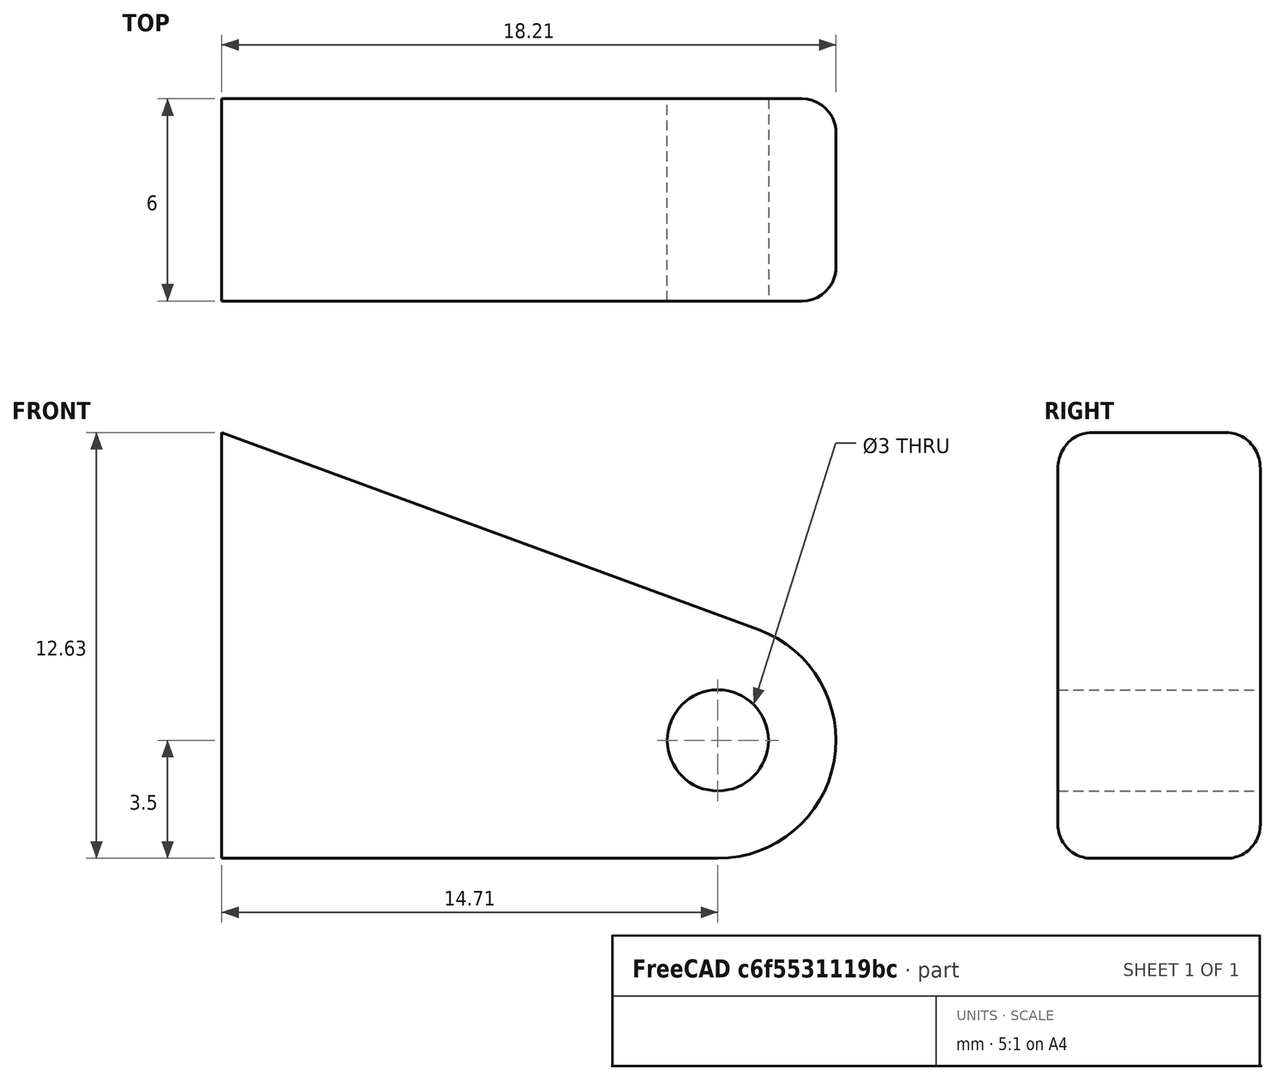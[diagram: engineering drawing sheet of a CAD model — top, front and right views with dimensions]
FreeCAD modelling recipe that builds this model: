
FCSTD DOCUMENT  (FreeCAD 0.16R6704 (Git))
Label: txerritxo
License: All rights reserved
LicenseURL: http://en.wikipedia.org/wiki/All_rights_reserved
objects: PartDesign::Fillet×2, Mesh::Feature×1, Part::Feature×1, Sketcher::SketchObject×1, PartDesign::Pad×1
note: 6 computed .brp shape members not serialized (recipe doc carries the construction recipe); baked Part::Feature solids carry a one-line shape summary decoded from their .brp

FEATURE [Mesh::Feature] SittingPiggy
FEATURE [Part::Feature] SittingPiggy001
  shape: bbox 33.54 x 35.04 x 27.84 mm, 16536 faces, 0 solids (baked)
FEATURE [Sketcher::SketchObject] Sketch
  Placement = pos=(0,0,0) rot=(1,0,0;1.5708rad)
  sketch-geometry (5):
    g0: Circle CenterX=16 CenterY=3.5 CenterZ=0 NormalX=0 NormalY=0 NormalZ=1 Radius=1.5
    g1: LineSegment StartX=16 StartY=0 StartZ=0 EndX=1.2919 EndY=0 EndZ=0
    g2: LineSegment StartX=1.2919 StartY=0 StartZ=0 EndX=1.2919 EndY=12.6301 EndZ=0
    g3: LineSegment StartX=1.2919 StartY=12.6301 StartZ=0 EndX=17.2066 EndY=6.78545 EndZ=0
    g4: ArcOfCircle CenterX=16 CenterY=3.5 CenterZ=0 NormalX=0 NormalY=0 NormalZ=1 Radius=3.5 StartAngle=4.71239 EndAngle=7.50202
  constraints (13):
    c: Radius(g0) = 1.5
    c: Coincident(g2,g1)
    c: Vertical(g2)
    c: Coincident(g3,g2)
    c: Coincident(g4,g0)
    c: Coincident(g4,g3)
    c: Coincident(g4,g1)
    c: Tangent(g3,g4)
    c: Tangent(g4,g1)
    c: Radius(g4) = 3.5
    c: DistanceX(g-1,g0) = 16
    c: PointOnObject(g1,g-1)
    c: Horizontal(g1)
FEATURE [PartDesign::Pad] Pad
  Length = 3
  Length2 = 3
  Placement = pos=(0,0,0) rot=(1,0,0;1.5708rad)
  Sketch = -> Sketch
  Type = 4
FEATURE [PartDesign::Fillet] Fillet
  Base = -> Pad [Edge10]
  Placement = pos=(0,0,0) rot=(1,0,0;1.5708rad)
  Radius = 1
FEATURE [PartDesign::Fillet] Fillet001
  Base = -> Fillet [Edge12]
  Placement = pos=(0,0,0) rot=(1,0,0;1.5708rad)
  Radius = 1
